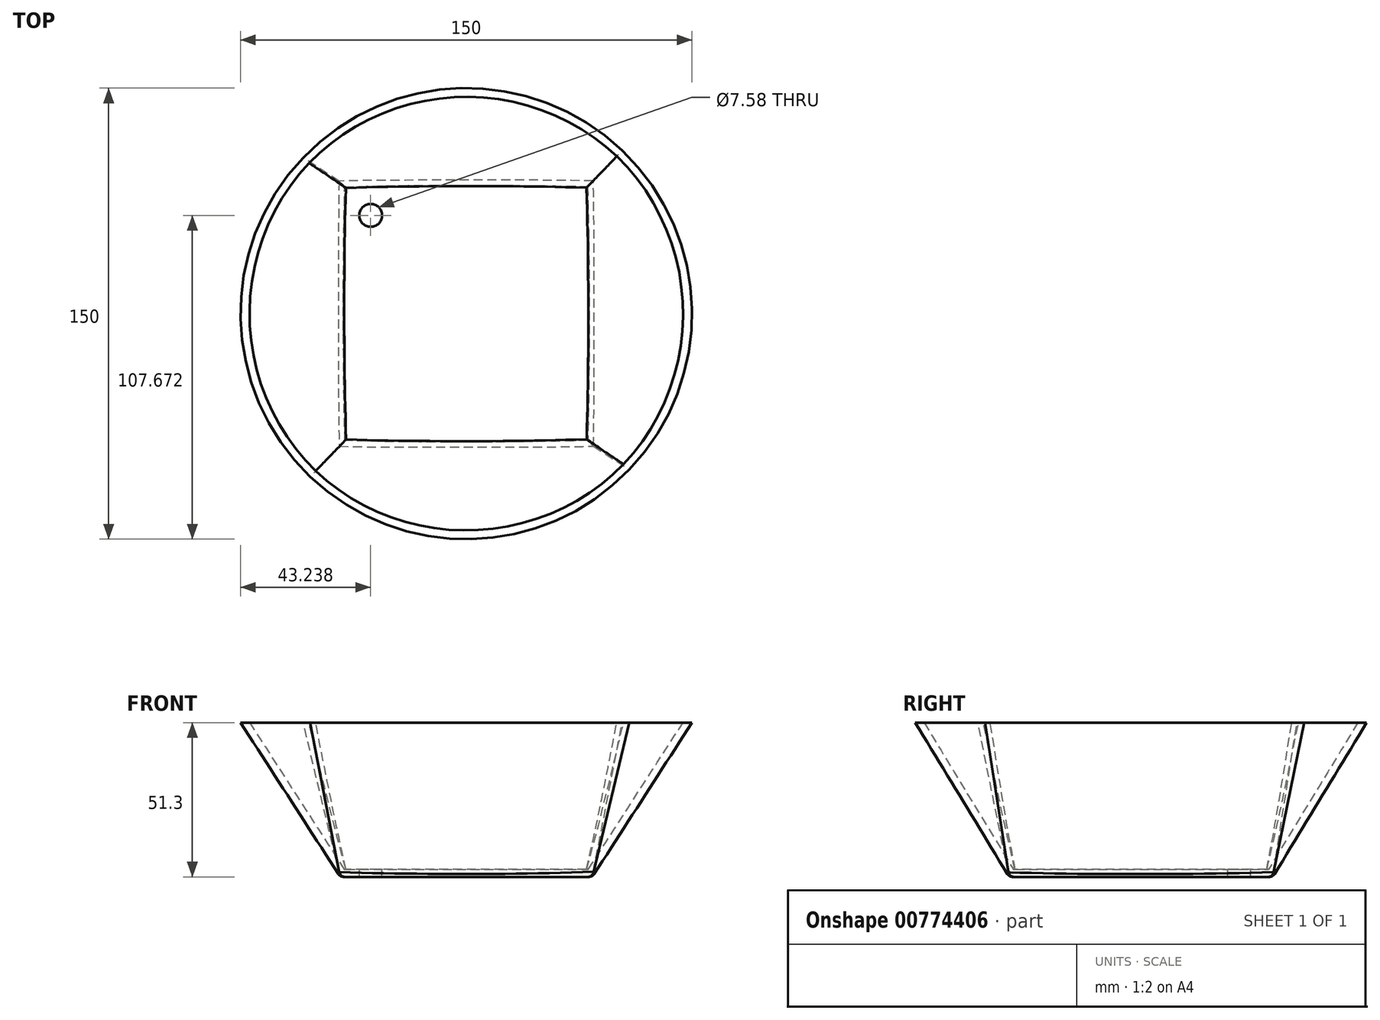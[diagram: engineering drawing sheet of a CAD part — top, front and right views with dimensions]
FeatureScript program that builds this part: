
annotation { "Feature Type Name" : "Feature", "Feature Type Description" : "" }
export const myFeature = defineFeature(function(context is Context, id is Id, definition is map)
    precondition{}
    {
        {
            var Q0;
            Q0=qCreatedBy(makeId("Top.planeOp"),FACE);
            var sketch = newSketch(context, id + "F0", { "sketchPlane" : qUnion([Q0])});
            skLineSegment(sketch, "E0.bottom", {"start": v(41.9, 43.81) * mm, "end": v(-41.9, 43.81) * mm});
            skLineSegment(sketch, "E0.top", {"start": v(41.9, -43.81) * mm, "end": v(-41.9, -43.81) * mm});
            skLineSegment(sketch, "E0.left", {"start": v(41.9, 43.81) * mm, "end": v(41.9, -43.81) * mm});
            skLineSegment(sketch, "E0.right", {"start": v(-41.9, 43.81) * mm, "end": v(-41.9, -43.81) * mm});
            skPoint(sketch, "E0.middle", {"position": v(0, 0) * mm});
            skSolve(sketch);
        }
        {
            var Q0;
            Q0=qCreatedBy(makeId("Top.planeOp"),FACE);
            cPlane(context, id + "F1", {"entities" : qUnion([Q0]), "cplaneType" : CPlaneType.OFFSET, "offset" : 51.3 * mm, "width" : 150 * mm, "height" : 150 * mm});
        }
        {
            var Q0;
            Q0=qCreatedBy(id+"F1.planeOp",FACE);
            var sketch = newSketch(context, id + "F2", { "sketchPlane" : qUnion([Q0])});
            skCircle(sketch, "E1", {"center": v(0, 0) * mm, "radius": 75 * mm});
            skSolve(sketch);
        }
        {
            var Q0;
            Q0=makeQuery(id+"F0.imprint","IMPRINT",FACE,{"disambiguationData":[TD([[makeQuery(id+"F0.imprint","IMPRINT",EDGE,{"derivedFrom":sQuery(id+"F0.wireOp",EDGE,"E0.bottom")}),1.0]])]});
            var Q1;
            Q1=makeQuery(id+"F2.imprint","IMPRINT",FACE,{"disambiguationData":[TD([[makeQuery(id+"F2.imprint","IMPRINT",EDGE,{"derivedFrom":sQuery(id+"F2.wireOp",EDGE,"E1")}),1.0]])]});
            loft(context, id + "F3", {"sheetProfilesArray" : [{ "sheetProfileEntities" : qUnion([Q0]) }, { "sheetProfileEntities" : qUnion([Q1]) }]});
        }
        {
            var Q0;
            Q0=makeQuery(id+"F3.opLoft","CAP_FACE",FACE,{"disambiguationData":[OSD([makeQuery(id+"F2.imprint","IMPRINT",FACE,{"disambiguationData":[TD([[makeQuery(id+"F2.imprint","IMPRINT",EDGE,{"derivedFrom":sQuery(id+"F2.wireOp",EDGE,"E1")}),1.0]])]})])],"isStart":true});
            shell(context, id + "F4", {"entities" : qUnion([Q0]), "thickness" : 2.5 * mm});
        }
        {
            var Q0;
            Q0=makeQuery(id+"F4.opShell","OFFSET_FACE",FACE,{"disambiguationData":[OSD([makeQuery(id+"F0.imprint","IMPRINT",FACE,{"disambiguationData":[TD([[makeQuery(id+"F0.imprint","IMPRINT",EDGE,{"derivedFrom":sQuery(id+"F0.wireOp",EDGE,"E0.bottom")}),1.0]])]})])]});
            var sketch = newSketch(context, id + "F5", { "sketchPlane" : qUnion([Q0])});
            skSolve(sketch);
        }
        {
            var Q0;
            {var subQ0=sQuery(id+"F0.wireOp",EDGE,"E0.right");var subQ1=sQuery(id+"F0.wireOp",EDGE,"E0.left");var subQ2=sQuery(id+"F0.wireOp",EDGE,"E0.bottom");Q0=makeQuery(id+"F5.imprint","IMPRINT",FACE,{"disambiguationData":[TD([[makeQuery(id+"F5.imprint","IMPRINT",EDGE,{"derivedFrom":makeQuery(id+"F4.opShell","OFFSET_EDGE",EDGE,{"disambiguationData":[OSD([subQ2,subQ1,subQ0])]})}),1.0]])]});}
            var sketch = newSketch(context, id + "F6", { "sketchPlane" : qUnion([Q0])});
            skCircle(sketch, "E2", {"center": v(-31.76, 32.67) * mm, "radius": 3.8 * mm});
            skSolve(sketch);
        }
        {
            var Q0;
            Q0 = qSketchRegion(id + "F6", true);
            extrude(context, id + "F7", {"entities" : qUnion([Q0]), "operationType" : NewBodyOperationType.REMOVE, "oppositeDirection" : true, "depth" : 25 * mm, "offsetDistance" : 25 * mm});
        }
        {
            var Q0;
            Q0=makeQuery(id+"F3.opLoft","MID_CAP_EDGE",EDGE,{"disambiguationData":[OSD([sQuery(id+"F0.wireOp",EDGE,"E0.bottom"),sQuery(id+"F0.wireOp",EDGE,"E0.top"),sQuery(id+"F0.wireOp",EDGE,"E0.right")])],"capPos":0.0});
            var Q1;
            Q1=makeQuery(id+"F3.opLoft","MID_CAP_EDGE",EDGE,{"disambiguationData":[OSD([sQuery(id+"F0.wireOp",EDGE,"E0.top"),sQuery(id+"F0.wireOp",EDGE,"E0.left"),sQuery(id+"F0.wireOp",EDGE,"E0.right")])],"capPos":0.0});
            var Q2;
            Q2=makeQuery(id+"F3.opLoft","MID_CAP_EDGE",EDGE,{"disambiguationData":[OSD([sQuery(id+"F0.wireOp",EDGE,"E0.bottom"),sQuery(id+"F0.wireOp",EDGE,"E0.left"),sQuery(id+"F0.wireOp",EDGE,"E0.right")])],"capPos":0.0});
            var Q3;
            Q3=makeQuery(id+"F3.opLoft","MID_CAP_EDGE",EDGE,{"disambiguationData":[OSD([sQuery(id+"F0.wireOp",EDGE,"E0.bottom"),sQuery(id+"F0.wireOp",EDGE,"E0.top"),sQuery(id+"F0.wireOp",EDGE,"E0.left")])],"capPos":0.0});
            fillet(context, id + "F8", {"entities" : qUnion([Q0, Q1, Q2, Q3]), "radius" : 2 * mm, "tangentPropagation" : true, "allowEdgeOverflow" : false});
        }
    });
